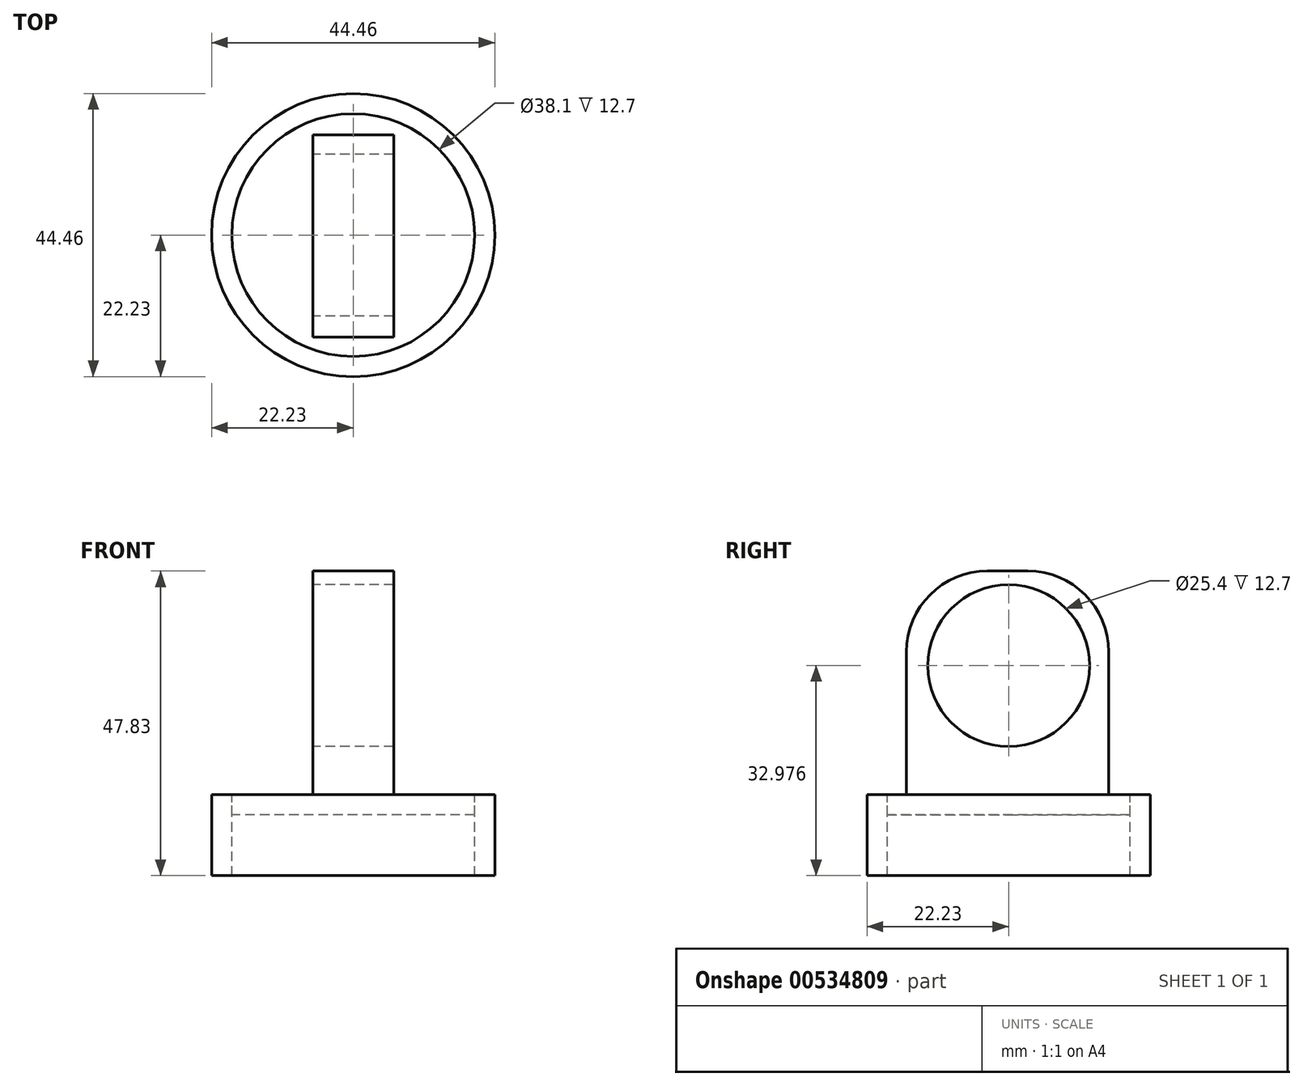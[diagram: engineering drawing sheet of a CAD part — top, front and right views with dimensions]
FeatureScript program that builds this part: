
annotation { "Feature Type Name" : "Feature", "Feature Type Description" : "" }
export const myFeature = defineFeature(function(context is Context, id is Id, definition is map)
    precondition{}
    {
        {
            var Q0;
            Q0=qCreatedBy(makeId("Right.planeOp"),FACE);
            var sketch = newSketch(context, id + "F0", { "sketchPlane" : qUnion([Q0])});
            skLineSegment(sketch, "E0.bottom", {"start": v(15.7, 0) * mm, "end": v(-16.04, 0) * mm});
            skLineSegment(sketch, "E0.top", {"start": v(3, 35.13) * mm, "end": v(-3.34, 35.13) * mm});
            skLineSegment(sketch, "E0.left", {"start": v(15.7, 0) * mm, "end": v(15.7, 22.43) * mm});
            skLineSegment(sketch, "E0.right", {"start": v(-16.04, 0) * mm, "end": v(-16.04, 22.43) * mm});
            skCircle(sketch, "E1", {"center": v(0, 20.28) * mm, "radius": 12.7 * mm});
            skPoint(sketch, "E2.visualSharp", {"position": v(15.7, 35.13) * mm});
            skArc(sketch, "E2.filletArc", {"start": v(15.7, 22.43) * mm, "mid": v(11.99, 31.4) * mm, "end": v(3, 35.13) * mm});
            skPoint(sketch, "E3.visualSharp", {"position": v(-16.04, 35.13) * mm});
            skArc(sketch, "E3.filletArc", {"start": v(-3.34, 35.13) * mm, "mid": v(-12.32, 31.4) * mm, "end": v(-16.04, 22.43) * mm});
            skSolve(sketch);
        }
        {
            var Q0;
            Q0=qCreatedBy(makeId("Top.planeOp"),FACE);
            var sketch = newSketch(context, id + "F1", { "sketchPlane" : qUnion([Q0])});
            skCircle(sketch, "E4", {"center": v(0, 0) * mm, "radius": 19.05 * mm});
            skCircle(sketch, "E5", {"center": v(0, 0) * mm, "radius": 22.23 * mm});
            skSolve(sketch);
        }
        {
            var Q0;
            Q0=makeQuery(id+"F0.imprint","IMPRINT",FACE,{"disambiguationData":[TD([[makeQuery(id+"F0.imprint","IMPRINT",EDGE,{"derivedFrom":sQuery(id+"F0.wireOp",EDGE,"E0.bottom")}),-1.0]])]});
            extrude(context, id + "F2", {"entities" : qUnion([Q0]), "depth" : 6.35 * mm, "offsetDistance" : 25.4 * mm});
        }
        {
            var Q0;
            Q0=makeQuery(id+"F2.opExtrude","CAP_FACE",FACE,{"disambiguationData":[OSD([sQuery(id+"F0.wireOp",EDGE,"E0.bottom"),sQuery(id+"F0.wireOp",EDGE,"E0.top"),sQuery(id+"F0.wireOp",EDGE,"E0.left"),sQuery(id+"F0.wireOp",EDGE,"E0.right"),sQuery(id+"F0.wireOp",EDGE,"E1")])],"isStart":true});
            extrude(context, id + "F3", {"entities" : qUnion([Q0]), "operationType" : NewBodyOperationType.ADD, "depth" : 6.35 * mm, "offsetDistance" : 25.4 * mm});
        }
        {
            var Q0;
            Q0=makeQuery(id+"F1.imprint","IMPRINT",FACE,{"disambiguationData":[TD([[makeQuery(id+"F1.imprint","IMPRINT",EDGE,{"derivedFrom":sQuery(id+"F1.wireOp",EDGE,"E4")}),-1.0]])]});
            extrude(context, id + "F4", {"entities" : qUnion([Q0]), "oppositeDirection" : true, "depth" : 12.7 * mm, "offsetDistance" : 25.4 * mm});
        }
        {
            var Q0;
            Q0=qCreatedBy(makeId("Top.planeOp"),FACE);
            var sketch = newSketch(context, id + "F5", { "sketchPlane" : qUnion([Q0])});
            skCircle(sketch, "E6", {"center": v(0, 0) * mm, "radius": 19.05 * mm});
            skSolve(sketch);
        }
        {
            var Q0;
            Q0=makeQuery(id+"F5.imprint","IMPRINT",FACE,{"disambiguationData":[TD([[makeQuery(id+"F5.imprint","IMPRINT",EDGE,{"derivedFrom":sQuery(id+"F5.wireOp",EDGE,"E6")}),1.0]])]});
            extrude(context, id + "F6", {"entities" : qUnion([Q0]), "oppositeDirection" : true, "depth" : 3.17 * mm, "offsetDistance" : 25.4 * mm});
        }
    });
